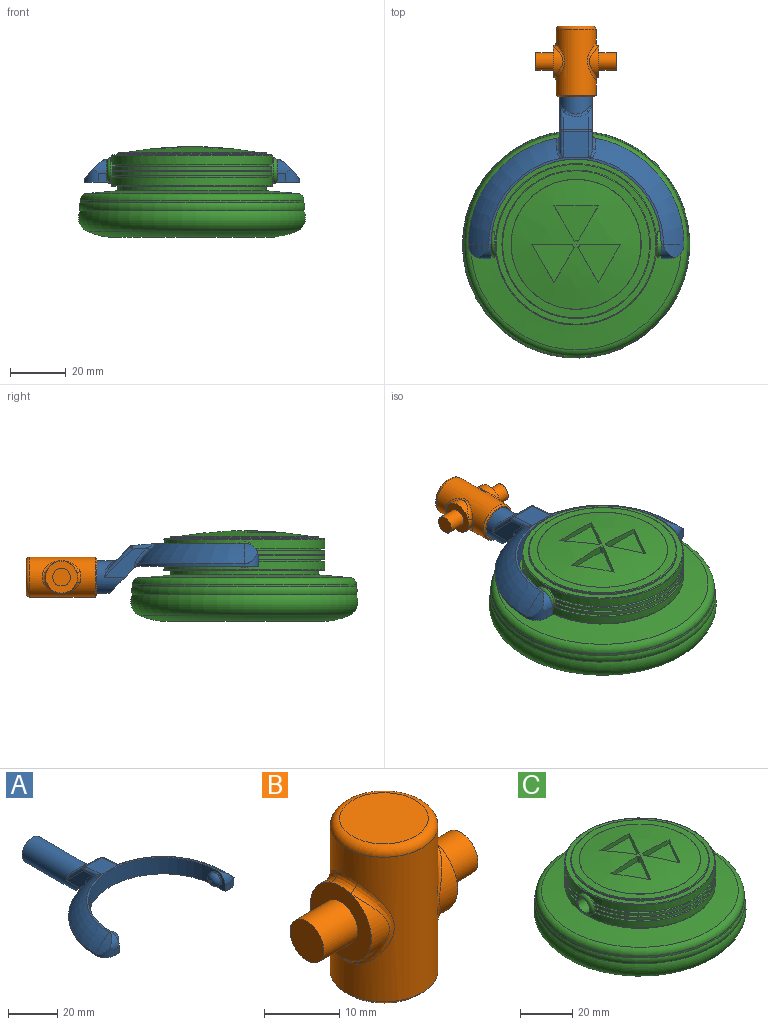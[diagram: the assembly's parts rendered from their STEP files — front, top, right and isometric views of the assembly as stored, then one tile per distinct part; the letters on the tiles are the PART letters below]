
ASSEMBLY  parts=3 mates=2
PART A: 48 faces, bbox 77.3x80.8x18.2 mm
  f0: plane 11.99x9.83mm, normal (0,-0.71,-0.71), area 141.5mm2, adj f1,f2,f9,f30,f43,f46
  f1: plane 15.39x10.49mm, normal (-1,0,0), area 63.5mm2, adj f0,f30,f32,f36,f46,f47
  f2: plane 15.39x10.49mm, normal (1,0,0), area 63.5mm2, adj f0,f30,f34,f39,f43,f44
  f3: plane 9.14x6.37mm, normal (0,0.71,0.71), area 67.6mm2, adj f35,f36,f39,f40
  f4: cylinder r=38.61mm len=37.99mm, axis (0,0,-1), area 42.6mm2, adj f6,f9,f17,f46,f47
  f5: torus R=19.3mm, axis (0,0,-1), area 507.8mm2, adj f10,f11,f12,f29,f42,f44
  f6: torus R=19.3mm, axis (0,0,-1), area 507.8mm2, adj f4,f11,f15,f28,f45,f47
  f7: cylinder r=30.48mm len=60.96mm, axis (0,0,-1), area 746.6mm2, adj f8,f9,f11,f14,f21,f24
  f8: plane 8.13x5.08mm, normal (-1,0,0), area 19.9mm2, adj f7,f9,f13,f19,f24
  f9: plane 77.22x43.73mm, normal (0,0,-1), area 956.2mm2, adj f0,f4,f7,f8,f10,f13,f14,f16
  f10: cylinder r=38.61mm len=37.99mm, axis (0,0,-1), area 42.6mm2, adj f5,f9,f20,f43,f44
  f11: plane 62.55x30.95mm, normal (0,0,1), area 75mm2, adj f5,f6,f7,f18,f19,f27
  f12: cylinder r=22.71mm len=7.33mm, axis (0,1,0), area 24.8mm2, adj f5,f19,f20
  f13: plane 3.05x3.05mm, normal (0,-1,0), area 9.3mm2, adj f8,f9,f19,f20
  f14: plane 8.13x5.08mm, normal (1,0,0), area 19.9mm2, adj f7,f9,f16,f18,f21
  f15: cylinder r=22.71mm len=7.33mm, axis (0,1,0), area 24.8mm2, adj f6,f17,f18
  f16: plane 3.05x3.05mm, normal (0,-1,0), area 9.3mm2, adj f9,f14,f17,f18
  f17: cylinder r=5.08mm len=5.08mm, axis (0,0,-1), area 21.9mm2, adj f4,f9,f15,f16,f18
  f18: cylinder r=5.08mm len=5.08mm, axis (-1,0,0), area 21.9mm2, adj f11,f14,f15,f16,f17
  f19: cylinder r=5.08mm len=5.08mm, axis (-1,0,0), area 21.9mm2, adj f8,f11,f12,f13,f20
  f20: cylinder r=5.08mm len=5.08mm, axis (0,0,-1), area 21.9mm2, adj f9,f10,f12,f13,f19
  f21: cylinder r=3.17mm len=6.35mm, axis (-1,0,0), area 12.7mm2, adj f7,f14,f23
  f22: plane 1.27x1.27mm, normal (1,0,0), area 1.3mm2, adj f23
  f23: torus R=0.64mm, axis (1,0,0), area 56.5mm2, adj f21,f22
  f24: cylinder r=3.17mm len=6.35mm, axis (1,0,0), area 12.7mm2, adj f7,f8,f26
  f25: plane 1.27x1.27mm, normal (-1,0,0), area 1.3mm2, adj f26
  f26: torus R=0.64mm, axis (-1,0,0), area 56.5mm2, adj f24,f25
  f27: plane 9.86x9.36mm, normal (0,0.09,1), area 85.6mm2, adj f11,f28,f29,f32,f34,f35,f42,f45
  f28: plane 1.04x0.17mm, normal (0,-1,0), area 0mm2, adj f6,f27,f45
  f29: plane 1.04x0.17mm, normal (0,-1,0), area 0mm2, adj f5,f27,f42
  f30: cylinder r=5.84mm len=33.01mm, axis (0,-1,0), area 1029.7mm2, adj f0,f1,f2,f31,f38,f40,f41
  f31: plane 11.68x11.68mm, normal (0,1,0), area 107.2mm2, adj f30
  f32: cylinder r=1.27mm len=9.13mm, axis (0,-1,0.09), area 14.4mm2, adj f1,f27,f33,f45
  f33: sphere r=1.27mm, area 1.5mm2, adj f32,f35,f36
  f34: cylinder r=1.27mm len=9.13mm, axis (0,1,-0.09), area 14.4mm2, adj f2,f27,f37,f42
  f35: cylinder r=1.27mm len=9.14mm, axis (-1,0,0), area 8.1mm2, adj f3,f27,f33,f37
  f36: cylinder r=1.27mm len=10.91mm, axis (0,-0.71,0.71), area 23.1mm2, adj f1,f3,f33,f38
  f37: sphere r=1.27mm, area 1.5mm2, adj f34,f35,f39
  f38: bspline ~4.55x2.75mm, area 2.3mm2, adj f30,f36,f40
  f39: cylinder r=1.27mm len=10.91mm, axis (0,0.71,-0.71), area 23.1mm2, adj f2,f3,f37,f41
  f40: bspline ~9.14x2.56mm, area 10.7mm2, adj f3,f30,f38,f41
  f41: bspline ~5.23x3.53mm, area 2.3mm2, adj f30,f39,f40
  f42: bspline ~4.62x3.14mm, area 5.2mm2, adj f5,f27,f29,f34,f44
  f43: cylinder r=1.27mm len=1.74mm, axis (0,0,-1), area 1.9mm2, adj f0,f2,f9,f10,f44
  f44: bspline ~8.6x7.86mm, area 11.9mm2, adj f2,f5,f10,f42,f43
  f45: bspline ~4.62x3.14mm, area 5.2mm2, adj f6,f27,f28,f32,f47
  f46: cylinder r=1.27mm len=1.74mm, axis (0,0,-1), area 1.9mm2, adj f0,f1,f4,f9,f47
  f47: bspline ~8.6x7.86mm, area 11.9mm2, adj f1,f4,f6,f45,f46
PART B: 25 faces, bbox 28.9x15.5x25.4 mm
  f0: cylinder r=5.71mm len=10.81mm, axis (-1,0,0), area 26.2mm2, adj f5,f15
  f1: cylinder r=5.71mm len=10.81mm, axis (-1,0,0), area 26.2mm2, adj f8,f11
  f2: cylinder r=7.14mm len=23.5mm, axis (0,0,-1), area 763.2mm2, adj f9,f10,f11,f12,f13,f14,f15,f16
  f3: plane 11.75x11.75mm, normal (0,0,1), area 108.4mm2, adj f17
  f4: plane 13.02x13.02mm, normal (0,0,-1), area 16.3mm2, adj f22,f24
  f5: plane 11.46x11.46mm, normal (1,0,0), area 70.9mm2, adj f0,f6,f13,f16,f18
  f6: cylinder r=5.71mm len=10.81mm, axis (-1,0,0), area 26.2mm2, adj f5,f14
  f7: cylinder r=5.71mm len=10.81mm, axis (-1,0,0), area 26.2mm2, adj f8,f10
  f8: plane 11.46x11.46mm, normal (-1,0,0), area 70.9mm2, adj f1,f7,f9,f12,f20
  f9: bspline ~4.64x1.73mm, area 6.5mm2, adj f2,f8,f10,f11
  f10: bspline ~13.62x4.91mm, area 20.7mm2, adj f2,f7,f9,f12
  f11: bspline ~13.6x4.87mm, area 20.7mm2, adj f1,f2,f9,f12
  f12: bspline ~4.64x1.73mm, area 6.5mm2, adj f2,f8,f10,f11
  f13: bspline ~4.64x1.73mm, area 6.5mm2, adj f2,f5,f14,f15
  f14: bspline ~13.62x4.91mm, area 20.7mm2, adj f2,f6,f13,f16
  f15: bspline ~13.6x4.87mm, area 20.7mm2, adj f0,f2,f13,f16
  f16: bspline ~4.64x1.73mm, area 6.5mm2, adj f2,f5,f14,f15
  f17: torus R=5.87mm, axis (0,0,1), area 83.8mm2, adj f2,f3
  f18: cylinder r=3.17mm len=6.35mm, axis (-1,0,0), area 126.7mm2, adj f5,f19
  f19: plane 6.35x6.35mm, normal (1,0,0), area 31.7mm2, adj f18
  f20: cylinder r=3.17mm len=6.35mm, axis (1,0,0), area 126.7mm2, adj f8,f21
  f21: plane 6.35x6.35mm, normal (-1,0,0), area 31.7mm2, adj f20
  f22: cylinder r=6.1mm len=22.86mm, axis (0,0,-1), area 875.6mm2, adj f4,f23
  f23: plane 12.19x12.19mm, normal (0,0,-1), area 116.7mm2, adj f22
  f24: cone r=7.14mm half-angle=45deg, axis (0,0,1), area 38.5mm2, adj f2,f4
PART C: 64 faces, bbox 96.2x96.2x32.5 mm
  f0: cylinder r=28.87mm len=57.73mm, axis (0,0,-1), area 525mm2, adj f5,f6,f54,f55,f60
  f1: cylinder r=27.59mm len=54.62mm, axis (0,0,1), area 49.8mm2, adj f3,f6,f54,f55
  f2: cylinder r=27.59mm len=54.62mm, axis (0,0,1), area 49.8mm2, adj f4,f5,f54,f55
  f3: plane 57.11x24.62mm, normal (0,0,-1), area 102.4mm2, adj f1,f8,f54,f55
  f4: plane 57.11x24.62mm, normal (0,0,-1), area 102.4mm2, adj f2,f7,f54,f55
  f5: plane 57.2x24.94mm, normal (0,0,1), area 103.2mm2, adj f0,f2,f54,f55
  f6: plane 57.2x24.94mm, normal (0,0,1), area 103.2mm2, adj f0,f1,f54,f55
  f7: cylinder r=28.87mm len=57.11mm, axis (0,0,-1), area 103.9mm2, adj f4,f11,f54,f55
  f8: cylinder r=28.87mm len=57.11mm, axis (0,0,-1), area 103.9mm2, adj f3,f12,f54,f55
  f9: plane 57.01x24.3mm, normal (0,0,-1), area 101mm2, adj f14,f15,f54,f55
  f10: plane 57.01x24.3mm, normal (0,0,-1), area 101mm2, adj f13,f16,f54,f55
  f11: plane 57.01x24.32mm, normal (0,0,1), area 101mm2, adj f7,f14,f54,f55
  f12: plane 57.01x24.32mm, normal (0,0,1), area 101mm2, adj f8,f13,f54,f55
  f13: cylinder r=27.6mm len=54.44mm, axis (0,0,1), area 49.2mm2, adj f10,f12,f54,f55
  f14: cylinder r=27.6mm len=54.44mm, axis (0,0,1), area 49.2mm2, adj f9,f11,f54,f55
  f15: cylinder r=28.87mm len=57.08mm, axis (0,0,-1), area 103.8mm2, adj f9,f20,f54,f55
  f16: cylinder r=28.87mm len=57.08mm, axis (0,0,-1), area 103.8mm2, adj f10,f19,f54,f55
  f17: plane 57.16x24.81mm, normal (0,0,-1), area 102.3mm2, adj f22,f23,f54,f55
  f18: plane 57.16x24.81mm, normal (0,0,-1), area 102.3mm2, adj f21,f23,f54,f55
  f19: plane 57.08x24.54mm, normal (0,0,1), area 101.6mm2, adj f16,f21,f54,f55
  f20: plane 57.08x24.54mm, normal (0,0,1), area 101.6mm2, adj f15,f22,f54,f55
  f21: cylinder r=27.6mm len=54.6mm, axis (0,0,1), area 49.7mm2, adj f18,f19,f54,f55
  f22: cylinder r=27.6mm len=54.6mm, axis (0,0,1), area 49.7mm2, adj f17,f20,f54,f55
  f23: cylinder r=28.87mm len=57.73mm, axis (0,0,-1), area 561.7mm2, adj f17,f18,f54,f55,f61
  f24: sphere r=135.39mm, area 1385.3mm2, adj f38,f39,f40,f41,f43,f44,f45,f46
  f25: plane 39.33x39.33mm, normal (0,0,-1), area 1214.6mm2, adj f26
  f26: torus R=20.12mm, axis (0,0,-1), area 1429.3mm2, adj f25,f27
  f27: torus R=27.74mm, axis (0,0,-1), area 3542.1mm2, adj f26,f28
  f28: torus R=35.36mm, axis (0,0,-1), area 2180.1mm2, adj f27,f29
  f29: torus R=37.35mm, axis (0,0,-1), area 734.6mm2, adj f28,f30
  f30: cylinder r=40.06mm len=80.11mm, axis (0,0,-1), area 213.3mm2, adj f29,f34
  f31: cone r=26.57mm half-angle=85deg, axis (0,0,-1), area 2265mm2, adj f32,f34
  f32: cylinder r=26.57mm len=53.14mm, axis (0,0,-1), area 265mm2, adj f31,f33
  f33: plane 57.23x57.23mm, normal (0,0,-1), area 354.5mm2, adj f32,f60
  f34: torus R=37.52mm, axis (0,0,1), area 928.6mm2, adj f30,f31
  f35: cone r=26.57mm half-angle=87deg, axis (0,0,-1), area 475.4mm2, adj f62,f63
  f36: cylinder r=26.57mm len=53.14mm, axis (0,0,-1), area 92.3mm2, adj f37,f62
  f37: plane 57.23x57.23mm, normal (0,0,1), area 354.5mm2, adj f36,f61
  f38: cylinder r=1.27mm len=2.53mm, axis (0,0,1), area 3.4mm2, adj f24,f39,f41,f42
  f39: plane 12.65x7.3mm, normal (0.87,0.5,0), area 32.2mm2, adj f24,f38,f40,f42
  f40: plane 13.75x7.94mm, normal (-0.87,0.5,0), area 28mm2, adj f24,f39,f41,f42
  f41: plane 14.61x2.53mm, normal (0,-1,0), area 32.2mm2, adj f24,f38,f40,f42
  f42: plane 15.24x13.75mm, normal (0,0,1), area 108.3mm2, adj f38,f39,f40,f41
  f43: plane 12.65x7.3mm, normal (-0.87,0.5,0), area 32.2mm2, adj f24,f44,f46,f47
  f44: cylinder r=1.27mm len=2.53mm, axis (0,0,1), area 3.4mm2, adj f24,f43,f45,f47
  f45: plane 14.61x2.53mm, normal (0,-1,0), area 32.2mm2, adj f24,f44,f46,f47
  f46: plane 13.75x7.94mm, normal (0.87,0.5,0), area 28mm2, adj f24,f43,f45,f47
  f47: plane 15.24x13.75mm, normal (0,0,1), area 108.3mm2, adj f43,f44,f45,f46
  f48: plane 15.88x1.84mm, normal (0,-1,0), area 28mm2, adj f24,f49,f51,f52
  f49: plane 12.65x7.3mm, normal (0.87,0.5,0), area 32.2mm2, adj f24,f48,f50,f52
  f50: cylinder r=1.27mm len=2.53mm, axis (0,0,1), area 3.4mm2, adj f24,f49,f51,f52
  f51: plane 12.65x7.3mm, normal (-0.87,0.5,0), area 32.2mm2, adj f24,f48,f50,f52
  f52: plane 15.88x12.65mm, normal (0,0,1), area 108.3mm2, adj f48,f49,f50,f51
  f53: plane 6.6x6.6mm, normal (1,0,0), area 2.6mm2, adj f58,f59
  f54: cylinder r=4.57mm len=9.14mm, axis (-1,0,0), area 20.3mm2, adj f0,f1,f2,f3,f4,f5,f6,f7
  f55: cylinder r=4.57mm len=9.14mm, axis (-1,0,0), area 20.3mm2, adj f0,f1,f2,f3,f4,f5,f6,f7
  f56: plane 6.6x6.6mm, normal (-1,0,0), area 2.6mm2, adj f57,f59
  f57: torus R=3.3mm, axis (1,0,0), area 51.5mm2, adj f55,f56
  f58: torus R=3.3mm, axis (1,0,0), area 51.5mm2, adj f53,f54
  f59: cylinder r=3.17mm len=60.96mm, axis (1,0,0), area 1216.1mm2, adj f53,f56
  f60: torus R=28.61mm, axis (0,0,1), area 72.1mm2, adj f0,f33
  f61: torus R=28.61mm, axis (0,0,-1), area 72.1mm2, adj f23,f37
  f62: torus R=26.31mm, axis (0,0,1), area 64.2mm2, adj f35,f36
  f63: torus R=23.29mm, axis (0,0,1), area 4.5mm2, adj f24,f35
PLACE A t=(32.34,27.52,20.85)mm
PLACE B rot(axis=(-1,0,0),90deg) t=(32.34,80.3,16.88)mm
PLACE C t=(32.34,27.52,33.52)mm
MATE revolute A.f24 <-> C.f54  axis (-1,0,0) through (62.82,27.52,24.92)mm
MATE revolute B.f2 <-> A.f30  axis (0,-1,0) through (32.34,103.16,16.88)mm
